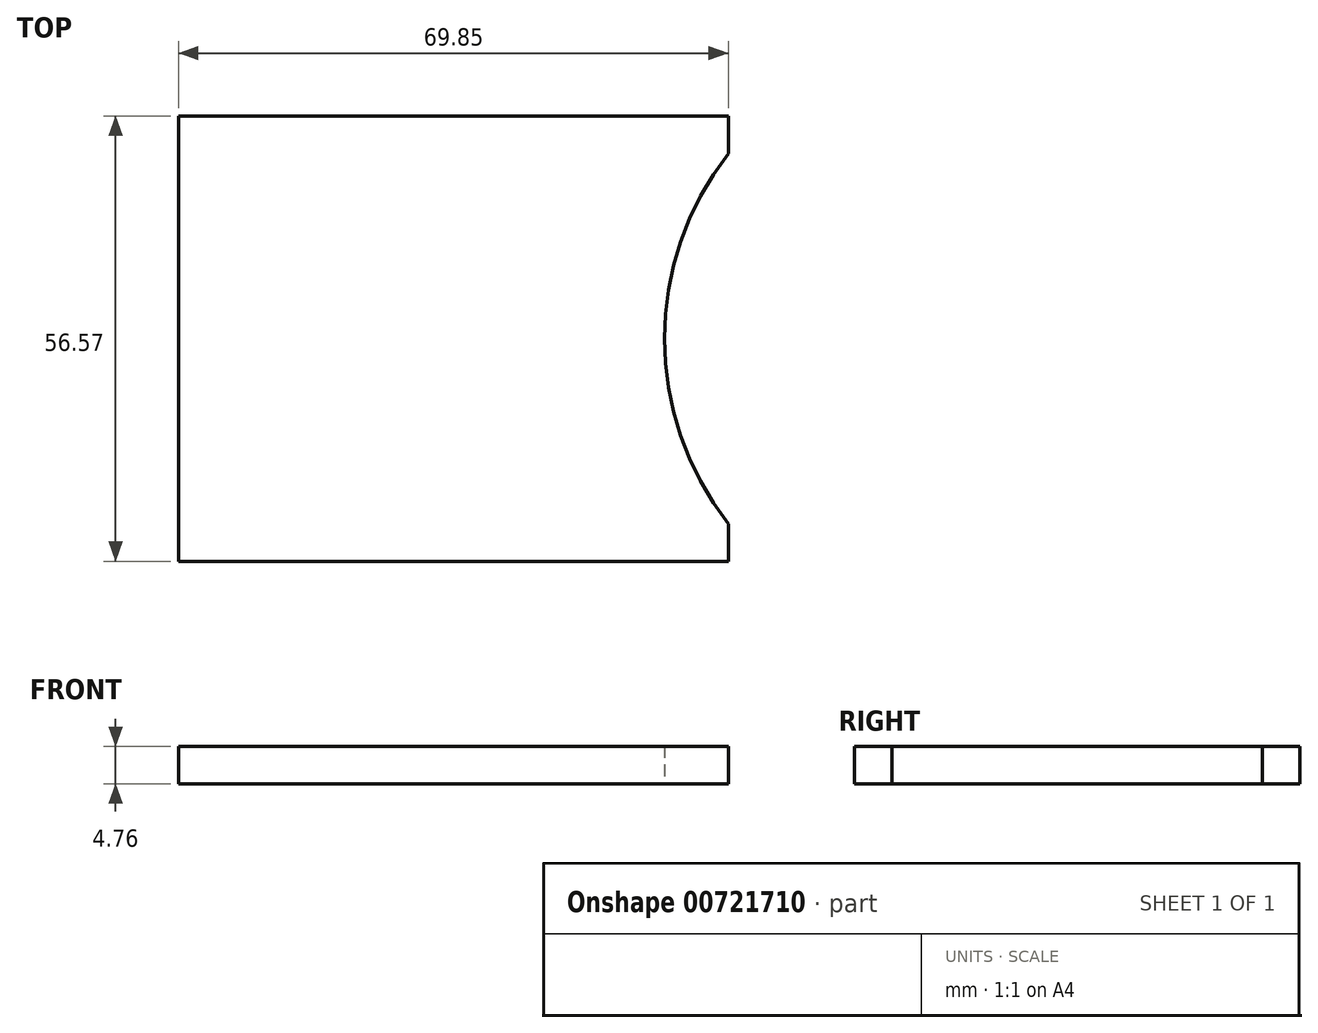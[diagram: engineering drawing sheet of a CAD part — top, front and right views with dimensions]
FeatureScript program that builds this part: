
annotation { "Feature Type Name" : "Feature", "Feature Type Description" : "" }
export const myFeature = defineFeature(function(context is Context, id is Id, definition is map)
    precondition{}
    {
        {
            var Q0;
            Q0=qCreatedBy(makeId("Top.planeOp"),FACE);
            var sketch = newSketch(context, id + "F0", { "sketchPlane" : qUnion([Q0])});
            skLineSegment(sketch, "E0.bottom", {"start": v(0, -56.57) * mm, "end": v(69.85, -56.57) * mm});
            skLineSegment(sketch, "E0.top", {"start": v(0, 0) * mm, "end": v(69.85, 0) * mm});
            skLineSegment(sketch, "E0.left", {"start": v(0, -56.57) * mm, "end": v(0, 0) * mm});
            skLineSegment(sketch, "E0.right", {"start": v(69.85, -56.57) * mm, "end": v(69.85, -51.8) * mm});
            skArc(sketch, "E1", {"start": v(69.85, -4.76) * mm, "mid": v(61.72, -28.28) * mm, "end": v(69.85, -51.8) * mm});
            skLineSegment(sketch, "E2.trimOffspring", {"start": v(69.85, -4.76) * mm, "end": v(69.85, 0) * mm});
            skSolve(sketch);
        }
        {
            var Q0;
            Q0=qSketchRegion(id+"F0",true);
            extrude(context, id + "F1", {"entities" : qUnion([Q0]), "depth" : 4.76 * mm, "offsetDistance" : 25.4 * mm});
        }
    });
